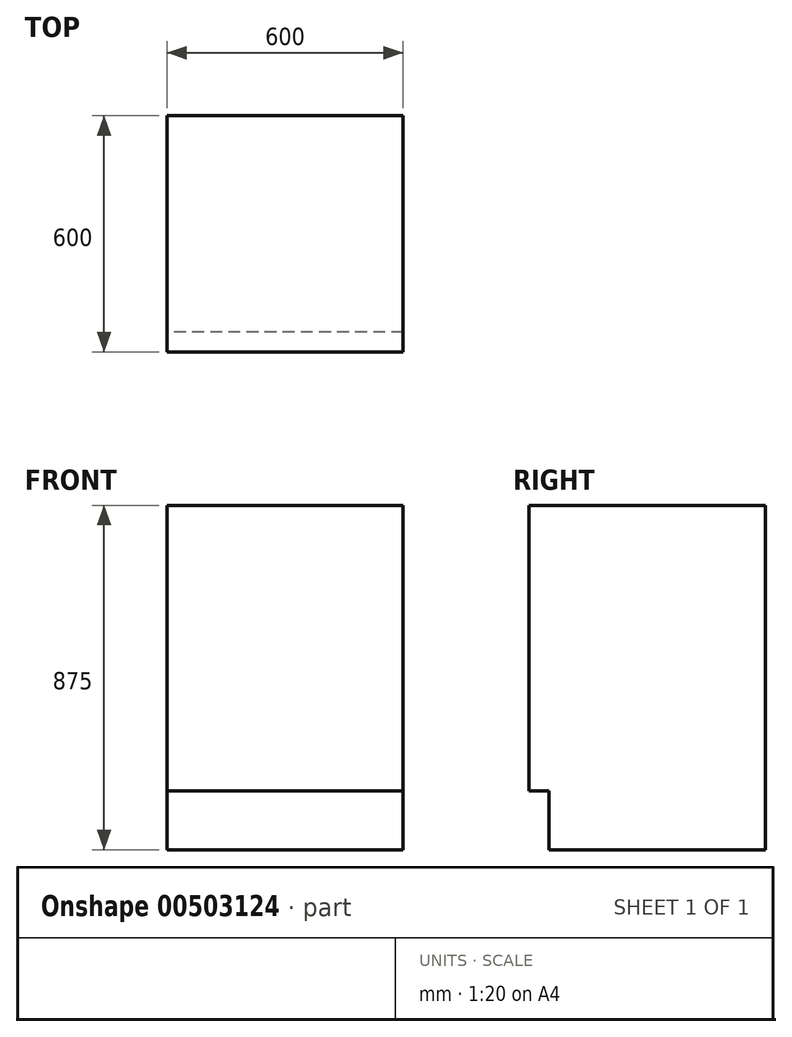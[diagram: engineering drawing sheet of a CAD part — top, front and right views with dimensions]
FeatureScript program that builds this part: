
annotation { "Feature Type Name" : "Feature", "Feature Type Description" : "" }
export const myFeature = defineFeature(function(context is Context, id is Id, definition is map)
    precondition{}
    {
        {
            var Q0;
            Q0=qCreatedBy(makeId("Right.planeOp"),FACE);
            var sketch = newSketch(context, id + "F0", { "sketchPlane" : qUnion([Q0])});
            skLineSegment(sketch, "E0", {"start": v(-600, 150) * mm, "end": v(-600, 875) * mm});
            skLineSegment(sketch, "E1", {"start": v(-600, 875) * mm, "end": v(0, 875) * mm});
            skLineSegment(sketch, "E2", {"start": v(0, 875) * mm, "end": v(0, 0) * mm});
            skLineSegment(sketch, "E3", {"start": v(0, 0) * mm, "end": v(-550, 0) * mm});
            skLineSegment(sketch, "E4", {"start": v(-600, 150) * mm, "end": v(-550, 150) * mm});
            skLineSegment(sketch, "E5", {"start": v(-550, 150) * mm, "end": v(-550, 0) * mm});
            skSolve(sketch);
        }
        {
            var Q0;
            Q0 = qSketchRegion(id + "F0", true);
            extrude(context, id + "F1", {"entities" : qUnion([Q0]), "flatOperationType" : FlatOperationType.REMOVE, "offsetDistance" : 25 * mm, "depth" : 600 * mm, "domain" : OperationDomain.MODEL});
        }
    });
